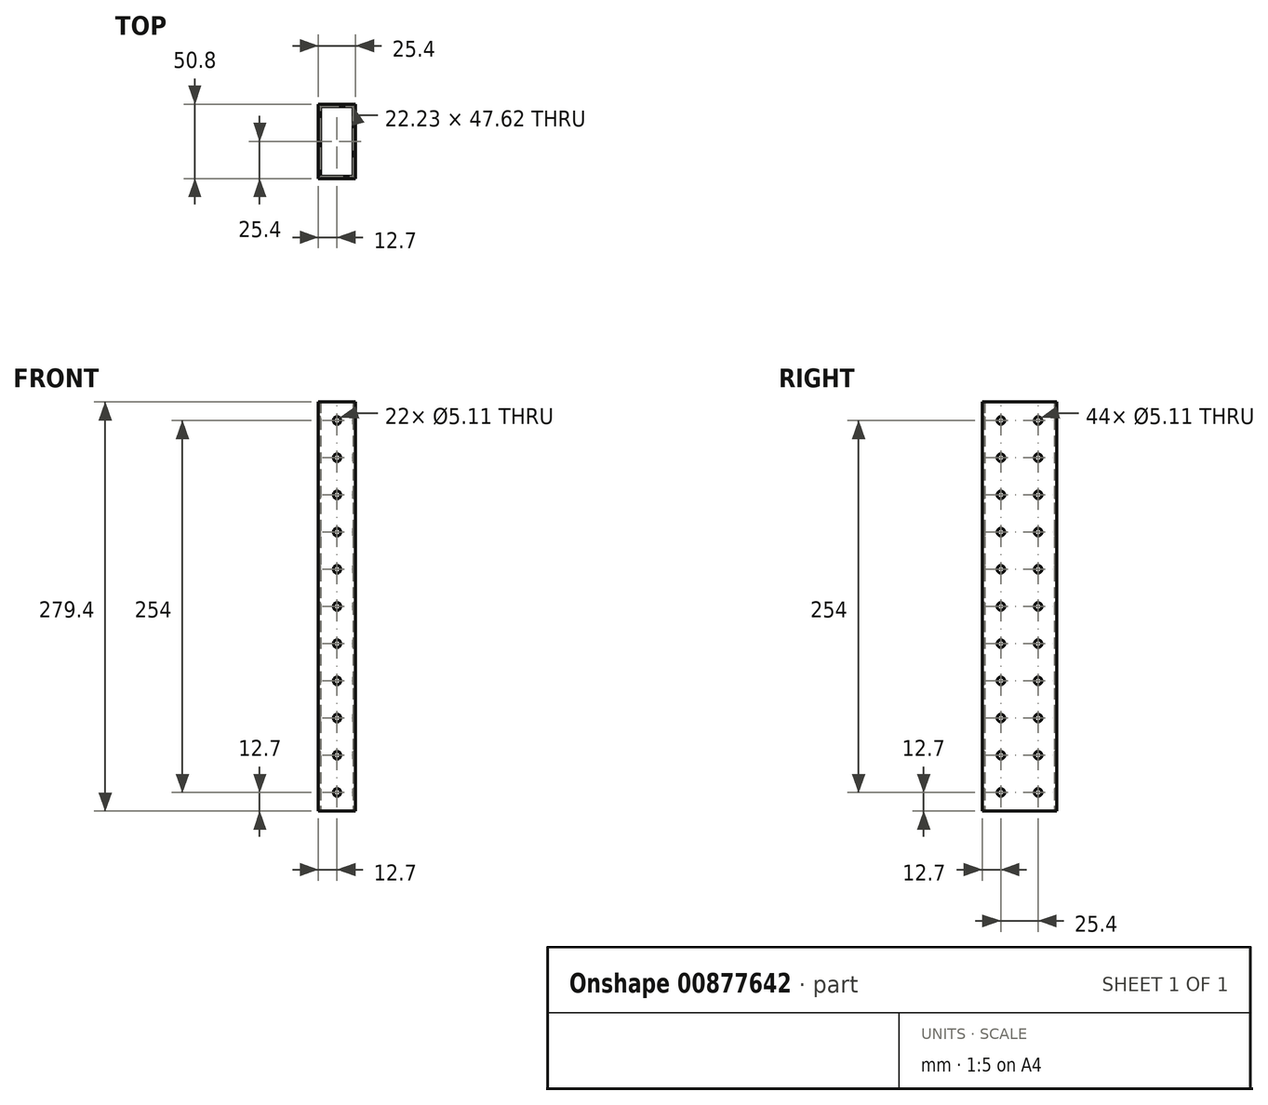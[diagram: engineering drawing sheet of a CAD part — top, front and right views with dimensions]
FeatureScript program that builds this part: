
annotation { "Feature Type Name" : "Feature", "Feature Type Description" : "" }
export const myFeature = defineFeature(function(context is Context, id is Id, definition is map)
    precondition{}
    {
        {
            var Q0;
            Q0=qCreatedBy(makeId("Top.planeOp"),FACE);
            var sketch = newSketch(context, id + "F0", { "sketchPlane" : qUnion([Q0])});
            skLineSegment(sketch, "E0.bottom", {"start": v(-12.7, 25.4) * mm, "end": v(12.7, 25.4) * mm});
            skLineSegment(sketch, "E0.top", {"start": v(-12.7, -25.4) * mm, "end": v(12.7, -25.4) * mm});
            skLineSegment(sketch, "E0.left", {"start": v(-12.7, 25.4) * mm, "end": v(-12.7, -25.4) * mm});
            skLineSegment(sketch, "E0.right", {"start": v(12.7, 25.4) * mm, "end": v(12.7, -25.4) * mm});
            skPoint(sketch, "E0.middle", {"position": v(0, 0) * mm});
            skLineSegment(sketch, "E1.0", {"start": v(-11.11, 23.81) * mm, "end": v(11.11, 23.81) * mm});
            skLineSegment(sketch, "E1.1", {"start": v(-11.11, 23.81) * mm, "end": v(-11.11, -23.81) * mm});
            skLineSegment(sketch, "E1.2", {"start": v(-11.11, -23.81) * mm, "end": v(11.11, -23.81) * mm});
            skLineSegment(sketch, "E1.3", {"start": v(11.11, 23.81) * mm, "end": v(11.11, -23.81) * mm});
            skSolve(sketch);
        }
        {
            var Q0;
            Q0=makeQuery(id+"F0.imprint","IMPRINT",FACE,{"disambiguationData":[TD([[makeQuery(id+"F0.imprint","IMPRINT",EDGE,{"derivedFrom":sQuery(id+"F0.wireOp",EDGE,"E0.bottom")}),-1.0]])]});
            extrude(context, id + "F1", {"entities" : qUnion([Q0]), "depth" : 279.4 * mm, "offsetDistance" : 25.4 * mm});
        }
        {
            var Q0;
            Q0=makeQuery(id+"F1.opExtrude","SWEPT_FACE",FACE,{"disambiguationData":[OSD([sQuery(id+"F0.wireOp",EDGE,"E0.top")])]});
            var sketch = newSketch(context, id + "F2", { "sketchPlane" : qUnion([Q0])});
            skCircle(sketch, "E2", {"center": v(0, 266.7) * mm, "radius": 2.55 * mm});
            skPoint(sketch, "E2.centerSnap0", {"position": v(0, 279.4) * mm});
            skLineSegment(sketch, "E3.direction1", {"start": v(0, 266.7) * mm, "end": v(25.4, 266.7) * mm, "construction": true});
            skLineSegment(sketch, "E3.direction2", {"start": v(0, 266.7) * mm, "end": v(0, 241.3) * mm, "construction": true});
            skCircle(sketch, "E4.0.0.1", {"center": v(0, 241.3) * mm, "radius": 2.55 * mm});
            skCircle(sketch, "E4.0.0.2", {"center": v(0, 215.9) * mm, "radius": 2.55 * mm});
            skCircle(sketch, "E4.0.0.3", {"center": v(0, 190.5) * mm, "radius": 2.55 * mm});
            skCircle(sketch, "E4.0.0.4", {"center": v(0, 165.1) * mm, "radius": 2.55 * mm});
            skCircle(sketch, "E4.0.0.5", {"center": v(0, 139.7) * mm, "radius": 2.55 * mm});
            skCircle(sketch, "E4.0.0.6", {"center": v(0, 114.3) * mm, "radius": 2.55 * mm});
            skCircle(sketch, "E4.0.0.7", {"center": v(0, 88.9) * mm, "radius": 2.55 * mm});
            skCircle(sketch, "E4.0.0.8", {"center": v(0, 63.5) * mm, "radius": 2.55 * mm});
            skCircle(sketch, "E4.0.0.9", {"center": v(0, 38.1) * mm, "radius": 2.55 * mm});
            skCircle(sketch, "E4.0.0.10", {"center": v(0, 12.7) * mm, "radius": 2.55 * mm});
            skSolve(sketch);
        }
        {
            var Q0;
            Q0 = qSketchRegion(id + "F2", true);
            extrude(context, id + "F3", {"entities" : qUnion([Q0]), "operationType" : NewBodyOperationType.REMOVE, "endBound" : BoundingType.THROUGH_ALL, "oppositeDirection" : true, "depth" : 25.4 * mm, "offsetDistance" : 25.4 * mm});
        }
        {
            var Q0;
            Q0=makeQuery(id+"F1.opExtrude","SWEPT_FACE",FACE,{"disambiguationData":[OSD([sQuery(id+"F0.wireOp",EDGE,"E0.left")])]});
            var sketch = newSketch(context, id + "F4", { "sketchPlane" : qUnion([Q0])});
            skCircle(sketch, "E5", {"center": v(-12.7, 12.7) * mm, "radius": 2.55 * mm});
            skCircle(sketch, "E6.1.0.0", {"center": v(12.7, 12.7) * mm, "radius": 2.55 * mm});
            skLineSegment(sketch, "E6.direction1", {"start": v(-12.7, 12.7) * mm, "end": v(12.7, 12.7) * mm, "construction": true});
            skLineSegment(sketch, "E6.direction2", {"start": v(-12.7, 12.7) * mm, "end": v(-12.7, 38.1) * mm, "construction": true});
            skCircle(sketch, "E7.0.0.1", {"center": v(-12.7, 38.1) * mm, "radius": 2.55 * mm});
            skCircle(sketch, "E7.0.0.2", {"center": v(-12.7, 63.5) * mm, "radius": 2.55 * mm});
            skCircle(sketch, "E7.0.0.3", {"center": v(-12.7, 88.9) * mm, "radius": 2.55 * mm});
            skCircle(sketch, "E7.0.0.4", {"center": v(-12.7, 114.3) * mm, "radius": 2.55 * mm});
            skCircle(sketch, "E7.0.0.5", {"center": v(-12.7, 139.7) * mm, "radius": 2.55 * mm});
            skCircle(sketch, "E7.0.0.6", {"center": v(-12.7, 165.1) * mm, "radius": 2.55 * mm});
            skCircle(sketch, "E7.0.0.7", {"center": v(-12.7, 190.5) * mm, "radius": 2.55 * mm});
            skCircle(sketch, "E7.0.0.8", {"center": v(-12.7, 215.9) * mm, "radius": 2.55 * mm});
            skCircle(sketch, "E7.0.0.9", {"center": v(-12.7, 241.3) * mm, "radius": 2.55 * mm});
            skCircle(sketch, "E7.0.0.10", {"center": v(-12.7, 266.7) * mm, "radius": 2.55 * mm});
            skCircle(sketch, "E7.0.1.1", {"center": v(12.7, 38.1) * mm, "radius": 2.55 * mm});
            skCircle(sketch, "E7.0.1.2", {"center": v(12.7, 63.5) * mm, "radius": 2.55 * mm});
            skCircle(sketch, "E7.0.1.3", {"center": v(12.7, 88.9) * mm, "radius": 2.55 * mm});
            skCircle(sketch, "E7.0.1.4", {"center": v(12.7, 114.3) * mm, "radius": 2.55 * mm});
            skCircle(sketch, "E7.0.1.5", {"center": v(12.7, 139.7) * mm, "radius": 2.55 * mm});
            skCircle(sketch, "E7.0.1.6", {"center": v(12.7, 165.1) * mm, "radius": 2.55 * mm});
            skCircle(sketch, "E7.0.1.7", {"center": v(12.7, 190.5) * mm, "radius": 2.55 * mm});
            skCircle(sketch, "E7.0.1.8", {"center": v(12.7, 215.9) * mm, "radius": 2.55 * mm});
            skCircle(sketch, "E7.0.1.9", {"center": v(12.7, 241.3) * mm, "radius": 2.55 * mm});
            skCircle(sketch, "E7.0.1.10", {"center": v(12.7, 266.7) * mm, "radius": 2.55 * mm});
            skSolve(sketch);
        }
        {
            var Q0;
            Q0 = qSketchRegion(id + "F4", true);
            extrude(context, id + "F5", {"entities" : qUnion([Q0]), "operationType" : NewBodyOperationType.REMOVE, "endBound" : BoundingType.THROUGH_ALL, "oppositeDirection" : true, "depth" : 25.4 * mm, "offsetDistance" : 25.4 * mm});
        }
    });
